# Revit family: 208_SGR-DA-_-_
name_source: partatom
category: Air Terminals
units: mm (PartAtom-declared; Revit-internal decimal feet)

## family parameters
Always vertical = Yes
Cut with Voids When Loaded = No
Part Type = Normal
Room Calculation Point = Yes
Round Connector Dimension = Use Diameter
Shared = No
Work Plane-Based = No

## types (14) — shared parameters
CAT0 = Yes
CL_Location_5000 = 5000 mm  [stored 16.4042 ft]
Description = STRAIGHT SLIDING DAMPER FOR SGR-0 & SGR-1 GRILLES
L_ARR = 400 mm  [stored 1.31234 ft]
Manufacturer = Alnor
URL = http://www.ventilation-alnor.co.uk
W_ARR = 400 mm  [stored 1.31234 ft]
XRefLineVPlnId = 7453
YRefLineVPlnId = 7456
magiPartTypeId = 208
magiProductFamilyId = SGR-DA-*-*
zero-valued in all types: CLBTZ, H_ARR

## per-type parameters (varying)
| type | B | BB | C | H | HH | H__ve | X1 |
| SGR-DA-325-75 | 325 mm | 163 mm | 55 mm  [stored 0.180446 ft] | 75 mm | 38 mm | -75 mm  [stored -0.246063 ft] | 33 mm  [stored 0.108268 ft] |
| SGR-DA-825-225 | 825 mm | 413 mm | 78 mm | 225 mm | 113 mm | -225 mm | 47 mm |
| SGR-DA-825-125 | 825 mm | 413 mm | 77 mm | 125 mm | 63 mm | -125 mm | 46 mm |
| SGR-DA-825-75 | 825 mm | 413 mm | 80 mm | 75 mm | 38 mm | -75 mm  [stored -0.246063 ft] | 48 mm |
| SGR-DA-625-225 | 625 mm | 313 mm | 78 mm | 225 mm | 113 mm | -225 mm | 47 mm |
| SGR-DA-625-125 | 625 mm | 313 mm | 75 mm  [stored 0.246063 ft] | 125 mm | 63 mm | -125 mm | 45 mm |
| SGR-DA-625-75 | 625 mm | 313 mm | 78 mm | 75 mm | 38 mm | -75 mm  [stored -0.246063 ft] | 47 mm |
| SGR-DA-525-225 | 525 mm | 263 mm | 70 mm | 225 mm | 113 mm | -225 mm | 42 mm |
| SGR-DA-525-125 | 525 mm | 263 mm | 70 mm | 125 mm | 63 mm | -125 mm | 42 mm |
| SGR-DA-525-75 | 525 mm | 263 mm | 70 mm | 75 mm | 38 mm | -75 mm  [stored -0.246063 ft] | 42 mm |
| SGR-DA-425-225 | 425 mm | 213 mm | 61 mm | 225 mm | 113 mm | -225 mm | 37 mm |
| SGR-DA-425-125 | 425 mm | 213 mm | 61 mm | 125 mm | 63 mm | -125 mm | 37 mm |
| SGR-DA-425-75 | 425 mm | 213 mm | 61 mm | 75 mm | 38 mm | -75 mm  [stored -0.246063 ft] | 37 mm |
| SGR-DA-325-125 | 325 mm | 163 mm | 40 mm | 125 mm | 63 mm | -125 mm | 24 mm |

note: column(s) folded — value = type name in every type: MC Product Code, magiProductId

note: [stored X ft] marks values corroborated as IEEE doubles in the binary element streams (Revit-internal decimal feet)

## geometry (parser evidence)
native form markers: Blend x4, Sweep x1
no freeform markers — native parametric forms only
